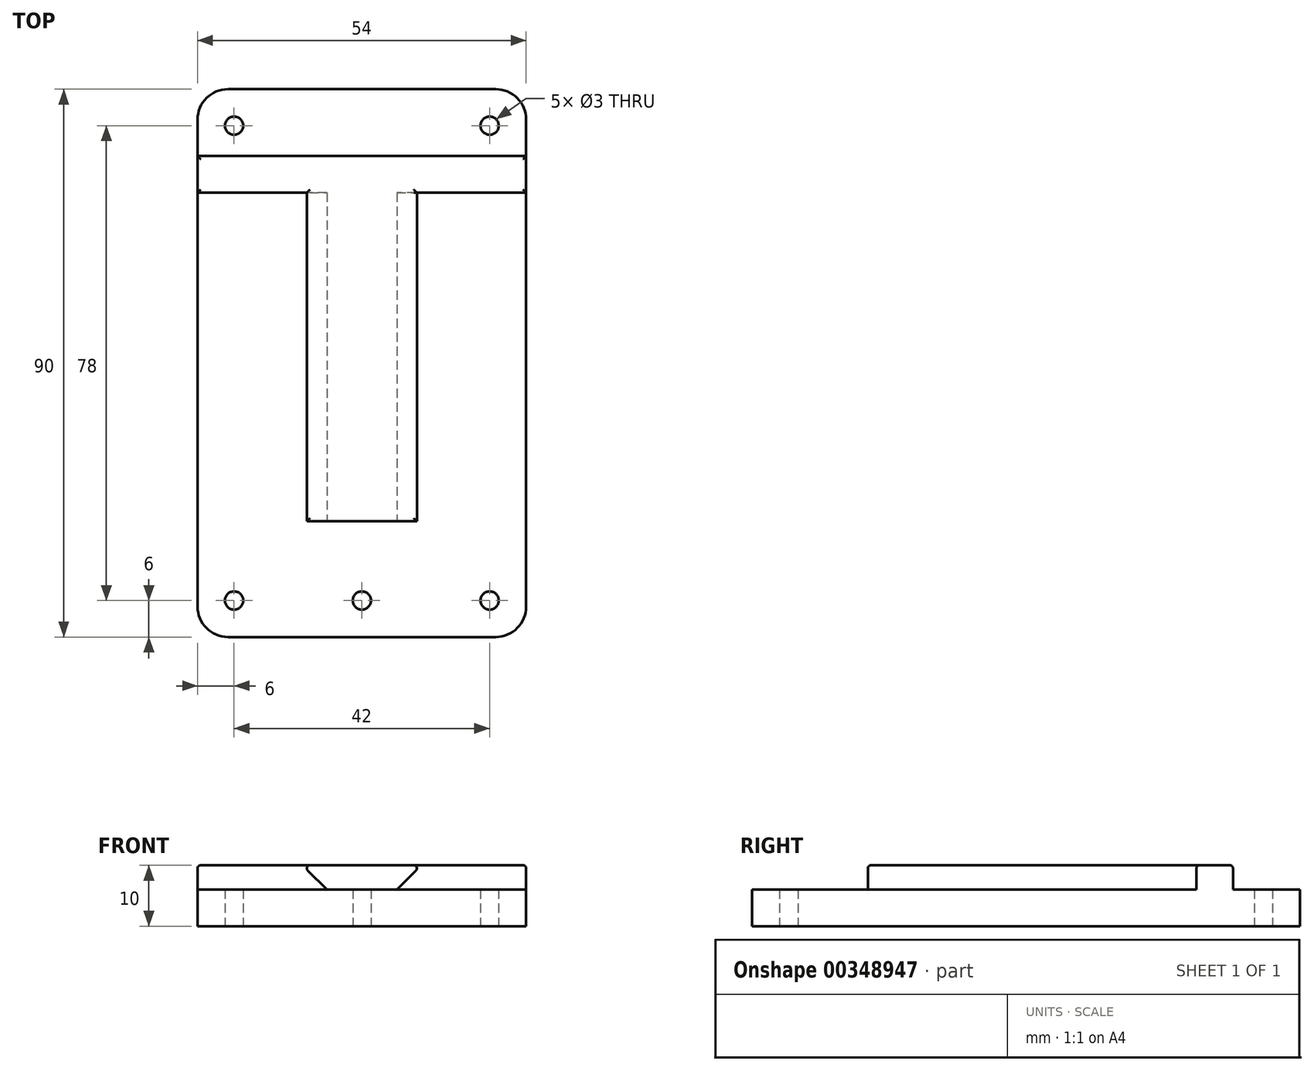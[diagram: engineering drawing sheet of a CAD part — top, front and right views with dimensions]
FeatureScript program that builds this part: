
annotation { "Feature Type Name" : "Feature", "Feature Type Description" : "" }
export const myFeature = defineFeature(function(context is Context, id is Id, definition is map)
    precondition{}
    {
        {
            var Q0;
            Q0=qCreatedBy(makeId("Top.planeOp"),FACE);
            var sketch = newSketch(context, id + "F0", { "sketchPlane" : qUnion([Q0])});
            skLineSegment(sketch, "E0.bottom", {"start": v(27, 45) * mm, "end": v(-27, 45) * mm});
            skLineSegment(sketch, "E0.top", {"start": v(27, -45) * mm, "end": v(-27, -45) * mm});
            skLineSegment(sketch, "E0.left", {"start": v(27, 45) * mm, "end": v(27, -45) * mm});
            skLineSegment(sketch, "E0.right", {"start": v(-27, 45) * mm, "end": v(-27, -45) * mm});
            skPoint(sketch, "E0.middle", {"position": v(0, 0) * mm});
            skSolve(sketch);
        }
        {
            var Q0;
            Q0=makeQuery(id+"F0.imprint","IMPRINT",FACE,{"disambiguationData":[TD([[makeQuery(id+"F0.imprint","IMPRINT",EDGE,{"derivedFrom":sQuery(id+"F0.wireOp",EDGE,"E0.bottom")}),1.0]])]});
            extrude(context, id + "F1", {"entities" : qUnion([Q0]), "depth" : 10 * mm});
        }
        {
            var Q0;
            Q0=makeQuery(id+"F1.opExtrude","SWEPT_FACE",FACE,{"disambiguationData":[OSD([sQuery(id+"F0.wireOp",EDGE,"E0.top")])]});
            var sketch = newSketch(context, id + "F2", { "sketchPlane" : qUnion([Q0])});
            skLineSegment(sketch, "E1.bottom", {"start": v(27, 6) * mm, "end": v(-27, 6) * mm, "construction": true});
            skLineSegment(sketch, "E1.top", {"start": v(27, 14) * mm, "end": v(-27, 14) * mm, "construction": true});
            skLineSegment(sketch, "E1.left", {"start": v(27, 6) * mm, "end": v(27, 14) * mm, "construction": true});
            skLineSegment(sketch, "E1.right", {"start": v(-27, 6) * mm, "end": v(-27, 14) * mm, "construction": true});
            skPoint(sketch, "E1.middle", {"position": v(0, 10) * mm});
            skLineSegment(sketch, "E2.bottom", {"start": v(9.75, 6) * mm, "end": v(-9.75, 6) * mm, "construction": true});
            skLineSegment(sketch, "E2.top", {"start": v(9.75, 14) * mm, "end": v(-9.75, 14) * mm, "construction": true});
            skLineSegment(sketch, "E2.left", {"start": v(9.75, 6) * mm, "end": v(9.75, 14) * mm, "construction": true});
            skLineSegment(sketch, "E2.right", {"start": v(-9.75, 6) * mm, "end": v(-9.75, 14) * mm, "construction": true});
            skLineSegment(sketch, "E3.bottom", {"start": v(5.75, 14) * mm, "end": v(-5.75, 14) * mm, "construction": true});
            skLineSegment(sketch, "E3.top", {"start": v(5.75, 6) * mm, "end": v(-5.75, 6) * mm, "construction": true});
            skLineSegment(sketch, "E3.left", {"start": v(5.75, 14) * mm, "end": v(5.75, 6) * mm, "construction": true});
            skLineSegment(sketch, "E3.right", {"start": v(-5.75, 14) * mm, "end": v(-5.75, 6) * mm, "construction": true});
            skLineSegment(sketch, "E4", {"start": v(-27, 6) * mm, "end": v(-5.75, 6) * mm});
            skLineSegment(sketch, "E5", {"start": v(-5.75, 6) * mm, "end": v(-9.75, 10) * mm});
            skLineSegment(sketch, "E6", {"start": v(5.75, 10) * mm, "end": v(-9.75, 10) * mm});
            skLineSegment(sketch, "E7", {"start": v(5.75, 10) * mm, "end": v(9.75, 10) * mm});
            skLineSegment(sketch, "E8", {"start": v(9.75, 10) * mm, "end": v(5.75, 6) * mm});
            skLineSegment(sketch, "E9", {"start": v(5.75, 6) * mm, "end": v(27, 6) * mm});
            skLineSegment(sketch, "E10", {"start": v(27, 6) * mm, "end": v(27, 10) * mm});
            skLineSegment(sketch, "E11", {"start": v(27, 10) * mm, "end": v(9.75, 10) * mm});
            skLineSegment(sketch, "E12", {"start": v(-27, 6) * mm, "end": v(-27, 10) * mm});
            skLineSegment(sketch, "E13", {"start": v(-27, 10) * mm, "end": v(-9.75, 10) * mm});
            skSolve(sketch);
        }
        {
            var Q0;
            Q0=makeQuery(id+"F2.imprint","IMPRINT",FACE,{"disambiguationData":[TD([[makeQuery(id+"F2.imprint","IMPRINT",EDGE,{"derivedFrom":sQuery(id+"F2.wireOp",EDGE,"E4")}),1.0]])]});
            var Q1;
            Q1=makeQuery(id+"F2.imprint","IMPRINT",FACE,{"disambiguationData":[TD([[makeQuery(id+"F2.imprint","IMPRINT",EDGE,{"derivedFrom":sQuery(id+"F2.wireOp",EDGE,"E8")}),1.0]])]});
            extrude(context, id + "F3", {"entities" : qUnion([Q0, Q1]), "operationType" : NewBodyOperationType.REMOVE, "oppositeDirection" : true, "depth" : 73 * mm});
        }
        {
            var Q0;
            Q0=makeQuery(id+"F1.opExtrude","CAP_FACE",FACE,{"disambiguationData":[OSD([sQuery(id+"F0.wireOp",EDGE,"E0.bottom"),sQuery(id+"F0.wireOp",EDGE,"E0.top"),sQuery(id+"F0.wireOp",EDGE,"E0.left"),sQuery(id+"F0.wireOp",EDGE,"E0.right")])],"isStart":true});
            var sketch = newSketch(context, id + "F4", { "sketchPlane" : qUnion([Q0])});
            skLineSegment(sketch, "E14.bottom", {"start": v(-27, 45) * mm, "end": v(-21, 45) * mm, "construction": true});
            skLineSegment(sketch, "E14.top", {"start": v(-27, 39) * mm, "end": v(-21, 39) * mm, "construction": true});
            skLineSegment(sketch, "E14.left", {"start": v(-27, 45) * mm, "end": v(-27, 39) * mm, "construction": true});
            skLineSegment(sketch, "E14.right", {"start": v(-21, 45) * mm, "end": v(-21, 39) * mm, "construction": true});
            skLineSegment(sketch, "E15.bottom", {"start": v(27, 45) * mm, "end": v(21, 45) * mm, "construction": true});
            skLineSegment(sketch, "E15.top", {"start": v(27, 39) * mm, "end": v(21, 39) * mm, "construction": true});
            skLineSegment(sketch, "E15.left", {"start": v(27, 45) * mm, "end": v(27, 39) * mm, "construction": true});
            skLineSegment(sketch, "E15.right", {"start": v(21, 45) * mm, "end": v(21, 39) * mm, "construction": true});
            skLineSegment(sketch, "E16.bottom", {"start": v(27, -45) * mm, "end": v(21, -45) * mm, "construction": true});
            skLineSegment(sketch, "E16.top", {"start": v(27, -39) * mm, "end": v(21, -39) * mm, "construction": true});
            skLineSegment(sketch, "E16.left", {"start": v(27, -45) * mm, "end": v(27, -39) * mm, "construction": true});
            skLineSegment(sketch, "E16.right", {"start": v(21, -45) * mm, "end": v(21, -39) * mm, "construction": true});
            skLineSegment(sketch, "E17.bottom", {"start": v(-27, -45) * mm, "end": v(-21, -45) * mm, "construction": true});
            skLineSegment(sketch, "E17.top", {"start": v(-27, -39) * mm, "end": v(-21, -39) * mm, "construction": true});
            skLineSegment(sketch, "E17.left", {"start": v(-27, -45) * mm, "end": v(-27, -39) * mm, "construction": true});
            skLineSegment(sketch, "E17.right", {"start": v(-21, -45) * mm, "end": v(-21, -39) * mm, "construction": true});
            skPoint(sketch, "E18", {"position": v(-21, 39) * mm});
            skPoint(sketch, "E19", {"position": v(21, 39) * mm});
            skPoint(sketch, "E20", {"position": v(21, -39) * mm});
            skPoint(sketch, "E21", {"position": v(-21, -39) * mm});
            skLineSegment(sketch, "E22", {"start": v(-21, 39) * mm, "end": v(0, 39) * mm, "construction": true});
            skPoint(sketch, "E23", {"position": v(0, 39) * mm});
            skSolve(sketch);
        }
        {
            var Q0;
            Q0=sQuery(id+"F4.wireOp",VERTEX,"E18");
            var Q1;
            Q1=sQuery(id+"F4.wireOp",VERTEX,"E19");
            var Q2;
            Q2=sQuery(id+"F4.wireOp",VERTEX,"E20");
            var Q3;
            Q3=sQuery(id+"F4.wireOp",VERTEX,"E21");
            var Q4;
            Q4=sQuery(id+"F4.wireOp",VERTEX,"E23");
            var Q5;
            Q5=makeQuery(id+"F1.opExtrude","SWEPT_BODY",BODY,{"disambiguationData":[OSD([sQuery(id+"F0.wireOp",EDGE,"E0.bottom"),sQuery(id+"F0.wireOp",EDGE,"E0.top"),sQuery(id+"F0.wireOp",EDGE,"E0.left"),sQuery(id+"F0.wireOp",EDGE,"E0.right")])]});
            hole(context, id + "F5", {"style" : HoleStyle.SIMPLE, "endStyle" : HoleEndStyle.THROUGH, "holeDiameter" : 3 * mm, "isTappedThrough" : true, "tappedDepth" : 12 * mm, "tapClearance" : 3, "locations" : qUnion([Q0, Q1, Q2, Q3, Q4]), "scope" : qUnion([Q5])});
        }
        {
            var Q0;
            Q0=makeQuery(id+"F1.opExtrude","SWEPT_FACE",FACE,{"disambiguationData":[OSD([sQuery(id+"F0.wireOp",EDGE,"E0.left")])]});
            var sketch = newSketch(context, id + "F6", { "sketchPlane" : qUnion([Q0])});
            skLineSegment(sketch, "E24.bottom", {"start": v(45, 10) * mm, "end": v(34, 10) * mm});
            skLineSegment(sketch, "E24.top", {"start": v(45, 6) * mm, "end": v(34, 6) * mm});
            skLineSegment(sketch, "E24.left", {"start": v(45, 10) * mm, "end": v(45, 6) * mm});
            skLineSegment(sketch, "E24.right", {"start": v(34, 10) * mm, "end": v(34, 6) * mm});
            skSolve(sketch);
        }
        {
            var Q0;
            Q0=makeQuery(id+"F6.imprint","IMPRINT",FACE,{"disambiguationData":[TD([[makeQuery(id+"F6.imprint","IMPRINT",EDGE,{"derivedFrom":sQuery(id+"F6.wireOp",EDGE,"E24.bottom")}),1.0]])]});
            extrude(context, id + "F7", {"entities" : qUnion([Q0]), "operationType" : NewBodyOperationType.REMOVE, "endBound" : BoundingType.THROUGH_ALL, "oppositeDirection" : true, "depth" : 25 * mm});
        }
        {
            var Q0;
            Q0=makeQuery(id+"F1.opExtrude","SWEPT_EDGE",EDGE,{"disambiguationData":[OSD([sQuery(id+"F0.wireOp",EDGE,"E0.top"),sQuery(id+"F0.wireOp",EDGE,"E0.left")])]});
            var Q1;
            Q1=makeQuery(id+"F1.opExtrude","SWEPT_EDGE",EDGE,{"disambiguationData":[OSD([sQuery(id+"F0.wireOp",EDGE,"E0.bottom"),sQuery(id+"F0.wireOp",EDGE,"E0.left")])]});
            var Q2;
            Q2=makeQuery(id+"F1.opExtrude","SWEPT_EDGE",EDGE,{"disambiguationData":[OSD([sQuery(id+"F0.wireOp",EDGE,"E0.bottom"),sQuery(id+"F0.wireOp",EDGE,"E0.right")])]});
            var Q3;
            Q3=makeQuery(id+"F1.opExtrude","SWEPT_EDGE",EDGE,{"disambiguationData":[OSD([sQuery(id+"F0.wireOp",EDGE,"E0.top"),sQuery(id+"F0.wireOp",EDGE,"E0.right")])]});
            fillet(context, id + "F8", {"entities" : qUnion([Q0, Q1, Q2, Q3]), "radius" : 5 * mm, "tangentPropagation" : true, "allowEdgeOverflow" : false});
        }
        {
            var Q0;
            Q0=makeQuery(id+"F1.opExtrude","CAP_FACE",FACE,{"disambiguationData":[OSD([sQuery(id+"F0.wireOp",EDGE,"E0.bottom"),sQuery(id+"F0.wireOp",EDGE,"E0.top"),sQuery(id+"F0.wireOp",EDGE,"E0.left"),sQuery(id+"F0.wireOp",EDGE,"E0.right")])],"isStart":false});
            var sketch = newSketch(context, id + "F9", { "sketchPlane" : qUnion([Q0])});
            skLineSegment(sketch, "E25.bottom", {"start": v(-9.75, -45) * mm, "end": v(9.75, -45) * mm});
            skLineSegment(sketch, "E25.top", {"start": v(-9.75, -26) * mm, "end": v(9.75, -26) * mm});
            skLineSegment(sketch, "E25.left", {"start": v(-9.75, -45) * mm, "end": v(-9.75, -26) * mm});
            skLineSegment(sketch, "E25.right", {"start": v(9.75, -45) * mm, "end": v(9.75, -26) * mm});
            skSolve(sketch);
        }
        {
            var Q0;
            Q0=makeQuery(id+"F9.imprint","IMPRINT",FACE,{"disambiguationData":[TD([[makeQuery(id+"F9.imprint","IMPRINT",EDGE,{"derivedFrom":sQuery(id+"F9.wireOp",EDGE,"E25.bottom")}),-1.0]])]});
            extrude(context, id + "F10", {"entities" : qUnion([Q0]), "operationType" : NewBodyOperationType.REMOVE, "oppositeDirection" : true, "depth" : 4 * mm});
        }
        {
            var Q0;
            Q0=makeQuery(id+"F3.boolean.opBoolean","COPY",EDGE,{"derivedFrom":makeQuery(id+"F3.opExtrude","SWEPT_EDGE",EDGE,{"disambiguationData":[OSD([sQuery(id+"F2.wireOp",EDGE,"E5"),sQuery(id+"F2.wireOp",EDGE,"E6"),sQuery(id+"F2.wireOp",EDGE,"E13")])]})});
            var Q1;
            Q1=makeQuery(id+"F3.boolean.opBoolean","COPY",EDGE,{"derivedFrom":makeQuery(id+"F3.opExtrude","SWEPT_EDGE",EDGE,{"disambiguationData":[OSD([sQuery(id+"F2.wireOp",EDGE,"E7"),sQuery(id+"F2.wireOp",EDGE,"E8"),sQuery(id+"F2.wireOp",EDGE,"E11")])]})});
            var Q2;
            Q2=makeQuery(id+"F3.boolean.opBoolean","COPY",EDGE,{"derivedFrom":makeQuery(id+"F3.opExtrude","CAP_EDGE",EDGE,{"disambiguationData":[OSD([sQuery(id+"F2.wireOp",EDGE,"E13")])],"isStart":false})});
            var Q3;
            Q3=makeQuery(id+"F3.boolean.opBoolean","COPY",EDGE,{"derivedFrom":makeQuery(id+"F3.opExtrude","CAP_EDGE",EDGE,{"disambiguationData":[OSD([sQuery(id+"F2.wireOp",EDGE,"E11")])],"isStart":false})});
            var Q4;
            Q4=makeQuery(id+"F1.opExtrude","CAP_FACE",FACE,{"disambiguationData":[OSD([sQuery(id+"F0.wireOp",EDGE,"E0.bottom"),sQuery(id+"F0.wireOp",EDGE,"E0.top"),sQuery(id+"F0.wireOp",EDGE,"E0.left"),sQuery(id+"F0.wireOp",EDGE,"E0.right")])],"isStart":false});
            fillet(context, id + "F11", {"entities" : qUnion([Q0, Q1, Q2, Q3, Q4]), "radius" : .5 * mm, "tangentPropagation" : true, "allowEdgeOverflow" : false});
        }
    });
